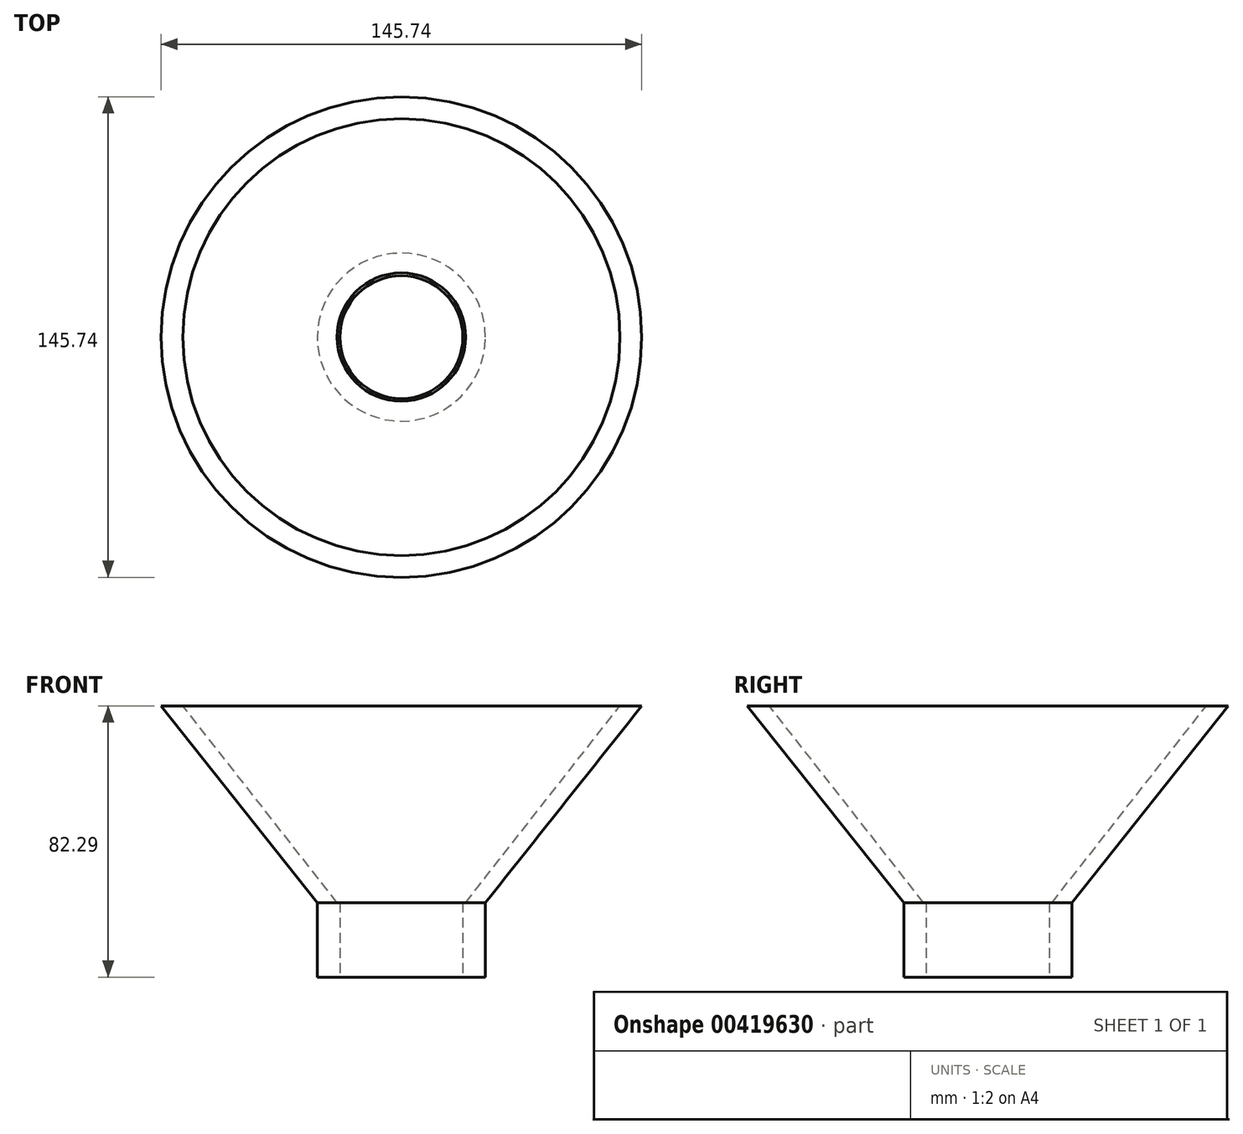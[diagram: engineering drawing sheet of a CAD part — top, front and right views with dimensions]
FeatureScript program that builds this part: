
annotation { "Feature Type Name" : "Feature", "Feature Type Description" : "" }
export const myFeature = defineFeature(function(context is Context, id is Id, definition is map)
    precondition{}
    {
        {
            var Q0;
            Q0=qCreatedBy(makeId("Front.planeOp"),FACE);
            var sketch = newSketch(context, id + "F0", { "sketchPlane" : qUnion([Q0])});
            skLineSegment(sketch, "E0", {"start": v(0, 0) * mm, "end": v(47.38, 59.68) * mm});
            skLineSegment(sketch, "E1", {"start": v(47.38, 59.68) * mm, "end": v(40.77, 59.68) * mm});
            skLineSegment(sketch, "E2", {"start": v(40.77, 59.68) * mm, "end": v(-6.02, 0) * mm});
            skLineSegment(sketch, "E3", {"start": v(-6.02, 0) * mm, "end": v(-25.5, 0) * mm});
            skLineSegment(sketch, "E4", {"start": v(-25.5, 0) * mm, "end": v(-25.5, -22.6) * mm});
            skLineSegment(sketch, "E5", {"start": v(-25.5, -22.6) * mm, "end": v(0, -22.6) * mm});
            skLineSegment(sketch, "E6", {"start": v(0, -22.6) * mm, "end": v(0, 0) * mm});
            skSolve(sketch);
        }
        {
            var Q0;
            Q0=makeQuery(id+"F0.imprint","IMPRINT",FACE,{"disambiguationData":[TD([[makeQuery(id+"F0.imprint","IMPRINT",EDGE,{"derivedFrom":sQuery(id+"F0.wireOp",EDGE,"E0")}),1.0]])]});
            var Q1;
            Q1=sQuery(id+"F0.wireOp",EDGE,"E4");
            var Q2;
            Q2=sQuery(id+"F0.wireOp",EDGE,"E4");
            revolve(context, id + "F1", {"entities" : qUnion([Q0]), "surfaceEntities" : qUnion([Q1]), "axis" : qUnion([Q2]), "revolveType" : RevolveType.FULL});
        }
        {
            var Q0;
            Q0=makeQuery(id+"F1.opRevolve","SWEPT_FACE",FACE,{"disambiguationData":[OSD([sQuery(id+"F0.wireOp",EDGE,"E5")])]});
            var sketch = newSketch(context, id + "F2", { "sketchPlane" : qUnion([Q0])});
            skCircle(sketch, "E7", {"center": v(-25.5, 0) * mm, "radius": 18.64 * mm});
            skSolve(sketch);
        }
        {
            var Q0;
            Q0=makeQuery(id+"F2.imprint","IMPRINT",FACE,{"disambiguationData":[TD([[makeQuery(id+"F2.imprint","IMPRINT",EDGE,{"derivedFrom":sQuery(id+"F2.wireOp",EDGE,"E7")}),1.0]])]});
            extrude(context, id + "F3", {"entities" : qUnion([Q0]), "operationType" : NewBodyOperationType.REMOVE, "oppositeDirection" : true, "depth" : 76.2 * mm});
        }
        {
            var Q0;
            Q0=makeQuery(id+"F1.opRevolve","SWEPT_FACE",FACE,{"disambiguationData":[OSD([sQuery(id+"F0.wireOp",EDGE,"E3")])]});
            var sketch = newSketch(context, id + "F4", { "sketchPlane" : qUnion([Q0])});
            skCircle(sketch, "E8", {"center": v(-25.5, 0) * mm, "radius": 15.88 * mm});
            skSolve(sketch);
        }
        {
            var Q0;
            Q0 = qSketchRegion(id + "F4", true);
            extrude(context, id + "F5", {"entities" : qUnion([Q0]), "operationType" : NewBodyOperationType.REMOVE, "oppositeDirection" : true, "depth" : 76.2 * mm});
        }
    });
